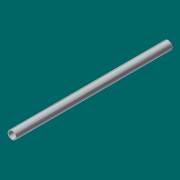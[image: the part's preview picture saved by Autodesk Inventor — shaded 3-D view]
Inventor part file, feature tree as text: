
AUTODESK INVENTOR PART (.ipt)
format: ipt  version: 2017 (Build 210142000, 142)  size: 100,864 bytes
history: native  units: in
note: dims shown in document units (in); Inventor stores cm internally (conversion verified against a paired STEP export)
features: extrude x1, sketch x1
ambient origin geometry x8: Origin, YZ Plane, XZ Plane, XY Plane, X Axis, Y Axis, Z Axis, Center Point
bodies: Solid1 (feature_tree)
feature tree (2):
  extrude  "Extrusion1"  Depth=54.25in
  sketch  "Sketch1"  dims[d0=2.875in d1=2.469in d2=54.25in d3=0.0in]
